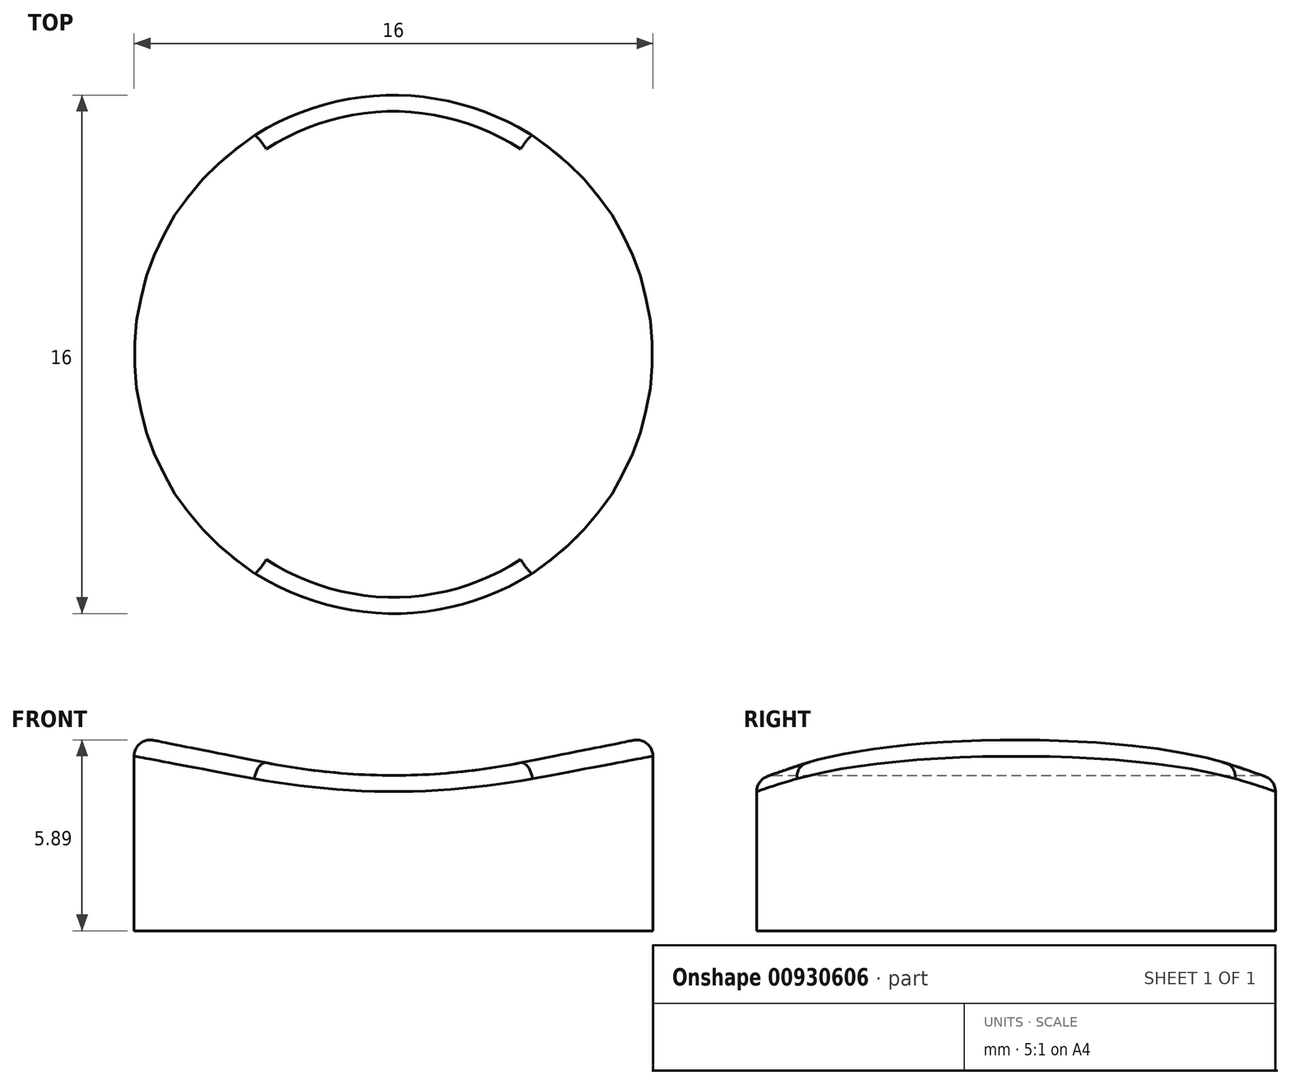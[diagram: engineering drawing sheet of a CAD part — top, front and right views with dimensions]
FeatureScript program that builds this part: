
annotation { "Feature Type Name" : "Feature", "Feature Type Description" : "" }
export const myFeature = defineFeature(function(context is Context, id is Id, definition is map)
    precondition{}
    {
        {
            var Q0;
            Q0=qCreatedBy(makeId("Top.planeOp"),FACE);
            var sketch = newSketch(context, id + "F0", { "sketchPlane" : qUnion([Q0])});
            skCircle(sketch, "E0", {"center": v(0, 0) * mm, "radius": 8 * mm});
            skSolve(sketch);
        }
        {
            var Q0;
            Q0=qSketchRegion(id+"F0",true);
            extrude(context, id + "F1", {"entities" : qUnion([Q0]), "depth" : 6 * mm, "offsetDistance" : 25 * mm});
        }
        {
            var Q0;
            Q0=qCreatedBy(makeId("Front.planeOp"),FACE);
            cPlane(context, id + "F2", {"entities" : qUnion([Q0]), "cplaneType" : CPlaneType.OFFSET, "offset" : 8 * mm, "width" : 150 * mm, "height" : 150 * mm});
        }
        {
            var Q0;
            Q0=qCreatedBy(id+"F2.planeOp",FACE);
            var sketch = newSketch(context, id + "F3", { "sketchPlane" : qUnion([Q0])});
            skLineSegment(sketch, "E1", {"start": v(-8, 6) * mm, "end": v(8, 6) * mm});
            skLineSegment(sketch, "E2", {"start": v(8, 6) * mm, "end": v(0, 4.4) * mm});
            skLineSegment(sketch, "E3", {"start": v(0, 4.4) * mm, "end": v(-8, 6) * mm});
            skSolve(sketch);
        }
        {
            var Q0;
            Q0=qSketchRegion(id+"F3",true);
            extrude(context, id + "F4", {"entities" : qUnion([Q0]), "operationType" : NewBodyOperationType.REMOVE, "endBound" : BoundingType.THROUGH_ALL, "oppositeDirection" : true, "depth" : 25 * mm, "offsetDistance" : 25 * mm});
        }
        {
            var Q0;
            Q0=makeQuery(id+"F4.boolean.opBoolean","COPY",EDGE,{"derivedFrom":makeQuery(id+"F4.opExtrude","SWEPT_EDGE",EDGE,{"disambiguationData":[OSD([sQuery(id+"F3.wireOp",EDGE,"E2"),sQuery(id+"F3.wireOp",EDGE,"E3")])]})});
            fillet(context, id + "F5", {"entities" : qUnion([Q0]), "radius" : 20 * mm, "tangentPropagation" : true, "allowEdgeOverflow" : false});
        }
        {
            var Q0;
            Q0=makeQuery(id+"F4.boolean.opBoolean","INTERSECT",EDGE,{"derivedFrom":[makeQuery(id+"F1.opExtrude","SWEPT_FACE",FACE,{"disambiguationData":[OSD([sQuery(id+"F0.wireOp",EDGE,"E0")])]}),makeQuery(id+"F4.opExtrude","SWEPT_FACE",FACE,{"disambiguationData":[OSD([sQuery(id+"F3.wireOp",EDGE,"E3")])]})]});
            fillet(context, id + "F6", {"entities" : qUnion([Q0]), "radius" : 0.5 * mm, "tangentPropagation" : true, "allowEdgeOverflow" : false});
        }
    });
